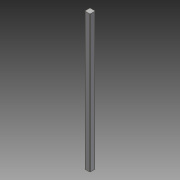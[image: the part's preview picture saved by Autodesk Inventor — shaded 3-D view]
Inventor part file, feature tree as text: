
AUTODESK INVENTOR PART (.ipt)
format: ipt  version: 2014 SP1 (Build 180222100, 222)  size: 76,800 bytes
history: native  units: in
note: dims shown in document units (in); Inventor stores cm internally (conversion verified against a paired STEP export)
features: extrude x1, fillet x1, sketch x1
ambient origin geometry x8: Origin, YZ Plane, XZ Plane, XY Plane, X Axis, Y Axis, Z Axis, Center Point
bodies: Solid1 (feature_tree)
feature tree (3):
  extrude  "Extrusion1"  Depth=0.0787in
  fillet  "Fillet1"  Radius=2.04in
  sketch  "Sketch1"  dims[d0=0.0787in d1=0.0787in d2=2.04in d3=0.0in d4=0.0079in]
